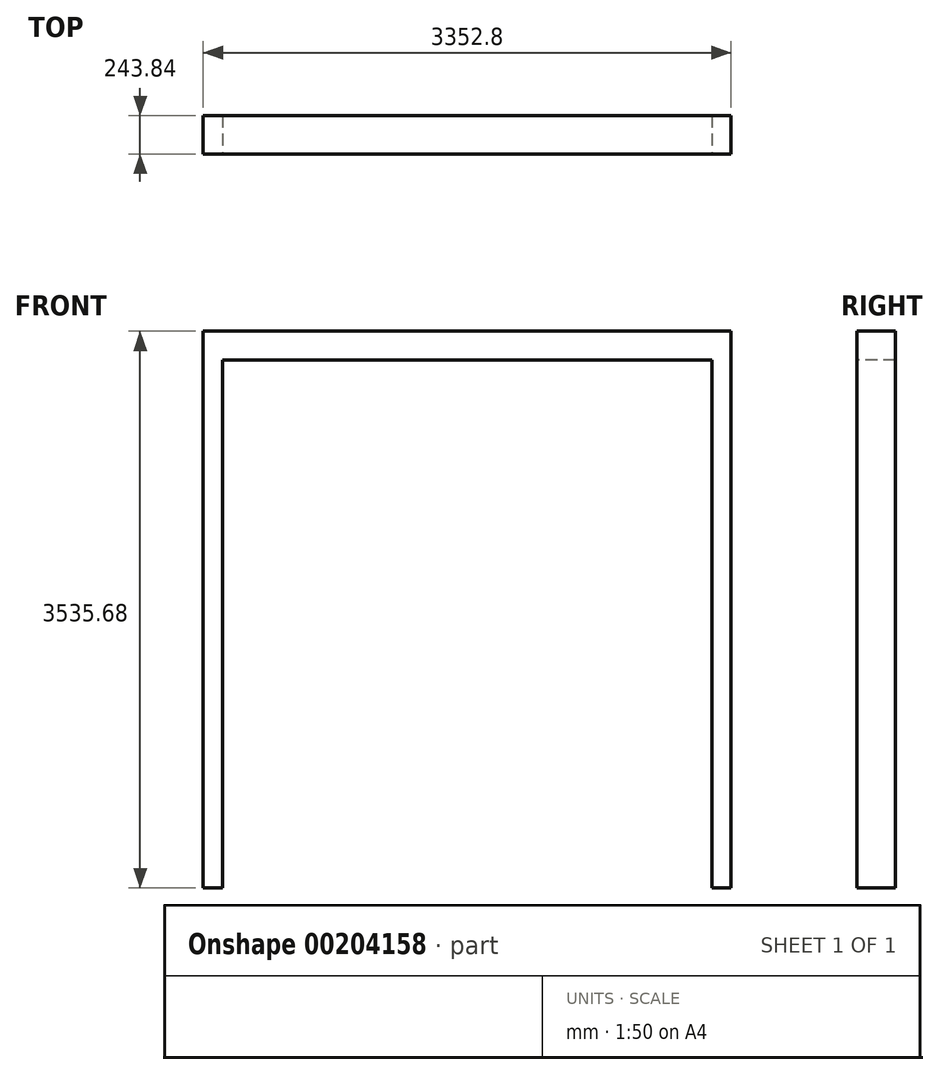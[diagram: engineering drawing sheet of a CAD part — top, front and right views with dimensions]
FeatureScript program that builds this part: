
annotation { "Feature Type Name" : "Feature", "Feature Type Description" : "" }
export const myFeature = defineFeature(function(context is Context, id is Id, definition is map)
    precondition{}
    {
        {
            var Q0;
            Q0=qCreatedBy(makeId("Top.planeOp"),FACE);
            var sketch = newSketch(context, id + "F0", { "sketchPlane" : qUnion([Q0])});
            skLineSegment(sketch, "E0.bottom", {"start": v(0, 0) * mm, "end": v(3352.8, 0) * mm});
            skLineSegment(sketch, "E0.top", {"start": v(0, -243.84) * mm, "end": v(3352.8, -243.84) * mm});
            skLineSegment(sketch, "E0.left", {"start": v(0, 0) * mm, "end": v(0, -243.84) * mm});
            skLineSegment(sketch, "E0.right", {"start": v(3352.8, 0) * mm, "end": v(3352.8, -243.84) * mm});
            skSolve(sketch);
        }
        {
            var Q0;
            Q0=makeQuery(id+"F0.imprint","IMPRINT",FACE,{"disambiguationData":[TD([[makeQuery(id+"F0.imprint","IMPRINT",EDGE,{"derivedFrom":sQuery(id+"F0.wireOp",EDGE,"E0.bottom")}),-1.0]])]});
            extrude(context, id + "F1", {"entities" : qUnion([Q0]), "depth" : 182.88 * mm});
        }
        {
            var Q0;
            Q0=makeQuery(id+"F1.opExtrude","CAP_FACE",FACE,{"disambiguationData":[OSD([sQuery(id+"F0.wireOp",EDGE,"E0.bottom"),sQuery(id+"F0.wireOp",EDGE,"E0.top"),sQuery(id+"F0.wireOp",EDGE,"E0.left"),sQuery(id+"F0.wireOp",EDGE,"E0.right")])],"isStart":true});
            var sketch = newSketch(context, id + "F2", { "sketchPlane" : qUnion([Q0])});
            skLineSegment(sketch, "E1.bottom", {"start": v(0, 0) * mm, "end": v(121.92, 0) * mm});
            skLineSegment(sketch, "E1.top", {"start": v(0, 243.84) * mm, "end": v(121.92, 243.84) * mm});
            skLineSegment(sketch, "E1.left", {"start": v(0, 0) * mm, "end": v(0, 243.84) * mm});
            skLineSegment(sketch, "E1.right", {"start": v(121.92, 0) * mm, "end": v(121.92, 243.84) * mm});
            skLineSegment(sketch, "E2.bottom", {"start": v(3230.88, 0) * mm, "end": v(3352.8, 0) * mm});
            skLineSegment(sketch, "E2.top", {"start": v(3230.88, 243.84) * mm, "end": v(3352.8, 243.84) * mm});
            skLineSegment(sketch, "E2.left", {"start": v(3230.88, 0) * mm, "end": v(3230.88, 243.84) * mm});
            skLineSegment(sketch, "E2.right", {"start": v(3352.8, 0) * mm, "end": v(3352.8, 243.84) * mm});
            skSolve(sketch);
        }
        {
            var Q0;
            Q0=makeQuery(id+"F2.imprint","IMPRINT",FACE,{"disambiguationData":[TD([[makeQuery(id+"F2.imprint","IMPRINT",EDGE,{"derivedFrom":sQuery(id+"F2.wireOp",EDGE,"E1.bottom")}),1.0]])]});
            var Q1;
            Q1=makeQuery(id+"F2.imprint","IMPRINT",FACE,{"disambiguationData":[TD([[makeQuery(id+"F2.imprint","IMPRINT",EDGE,{"derivedFrom":sQuery(id+"F2.wireOp",EDGE,"E2.bottom")}),1.0]])]});
            extrude(context, id + "F3", {"entities" : qUnion([Q0, Q1]), "operationType" : NewBodyOperationType.ADD, "depth" : 3352.8 * mm});
        }
    });
